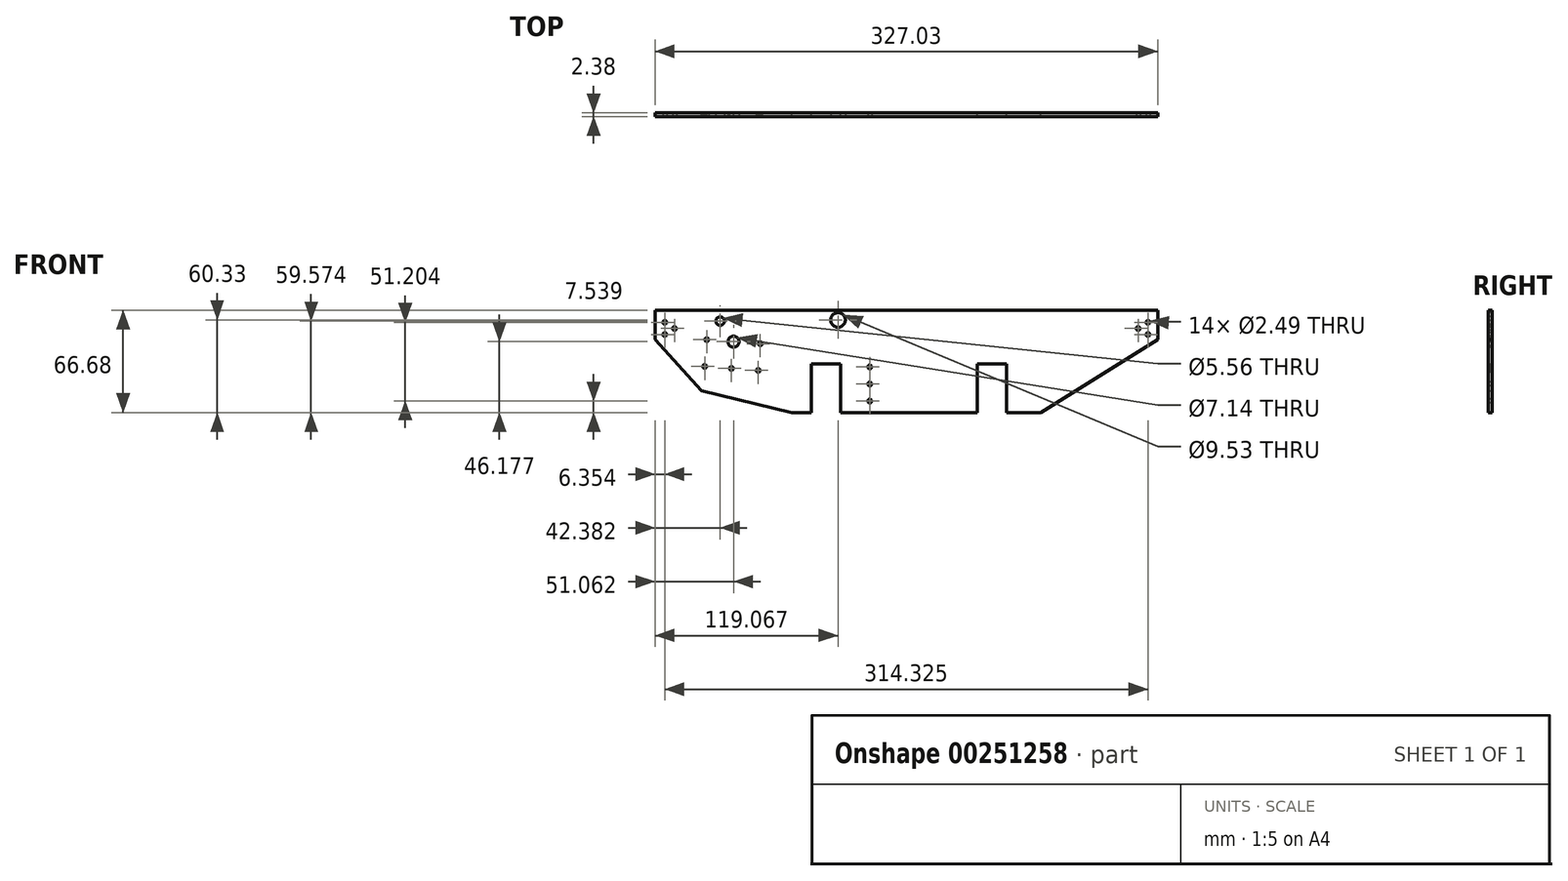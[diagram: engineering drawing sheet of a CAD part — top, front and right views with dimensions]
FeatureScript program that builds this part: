
annotation { "Feature Type Name" : "Feature", "Feature Type Description" : "" }
export const myFeature = defineFeature(function(context is Context, id is Id, definition is map)
    precondition{}
    {
        {
            var Q0;
            Q0=qCreatedBy(makeId("Front.planeOp"),FACE);
            var sketch = newSketch(context, id + "F0", { "sketchPlane" : qUnion([Q0])});
            skLineSegment(sketch, "E0", {"start": v(-44.67, 19.05) * mm, "end": v(282.36, 19.05) * mm});
            skLineSegment(sketch, "E1", {"start": v(282.36, 19.05) * mm, "end": v(282.36, 0) * mm});
            skLineSegment(sketch, "E2", {"start": v(282.36, 0) * mm, "end": v(206.16, -47.63) * mm});
            skLineSegment(sketch, "E3", {"start": v(206.16, -47.63) * mm, "end": v(183.93, -47.63) * mm});
            skLineSegment(sketch, "E4", {"start": v(183.93, -47.63) * mm, "end": v(183.93, -15.88) * mm});
            skLineSegment(sketch, "E5", {"start": v(183.93, -15.88) * mm, "end": v(164.88, -15.88) * mm});
            skLineSegment(sketch, "E6", {"start": v(164.88, -15.88) * mm, "end": v(164.88, -47.63) * mm});
            skLineSegment(sketch, "E7", {"start": v(164.88, -47.63) * mm, "end": v(75.98, -47.63) * mm});
            skLineSegment(sketch, "E8", {"start": v(75.98, -47.63) * mm, "end": v(75.98, -15.88) * mm});
            skLineSegment(sketch, "E9", {"start": v(75.98, -15.88) * mm, "end": v(56.93, -15.88) * mm});
            skLineSegment(sketch, "E10", {"start": v(56.93, -15.88) * mm, "end": v(56.93, -47.63) * mm});
            skLineSegment(sketch, "E11", {"start": v(56.93, -47.63) * mm, "end": v(44.23, -47.63) * mm});
            skLineSegment(sketch, "E12", {"start": v(44.23, -47.63) * mm, "end": v(-14.5, -33.4) * mm});
            skLineSegment(sketch, "E13", {"start": v(-14.5, -33.4) * mm, "end": v(-44.67, 0) * mm});
            skLineSegment(sketch, "E14", {"start": v(-44.67, 0) * mm, "end": v(-44.67, 19.05) * mm});
            skSolve(sketch);
        }
        {
            var Q0;
            Q0 = qSketchRegion(id + "F0", true);
            extrude(context, id + "F1", {"entities" : qUnion([Q0]), "depth" : 2.38 * mm});
        }
        {
            var Q0;
            Q0=makeQuery(id+"F1.opExtrude","CAP_FACE",FACE,{"disambiguationData":[OSD([sQuery(id+"F0.wireOp",EDGE,"E0"),sQuery(id+"F0.wireOp",EDGE,"E1"),sQuery(id+"F0.wireOp",EDGE,"E2"),sQuery(id+"F0.wireOp",EDGE,"E3"),sQuery(id+"F0.wireOp",EDGE,"E4"),sQuery(id+"F0.wireOp",EDGE,"E5"),sQuery(id+"F0.wireOp",EDGE,"E6"),sQuery(id+"F0.wireOp",EDGE,"E7"),sQuery(id+"F0.wireOp",EDGE,"E8"),sQuery(id+"F0.wireOp",EDGE,"E9"),sQuery(id+"F0.wireOp",EDGE,"E10"),sQuery(id+"F0.wireOp",EDGE,"E11"),sQuery(id+"F0.wireOp",EDGE,"E12"),sQuery(id+"F0.wireOp",EDGE,"E13"),sQuery(id+"F0.wireOp",EDGE,"E14")])],"isStart":false});
            var sketch = newSketch(context, id + "F2", { "sketchPlane" : qUnion([Q0])});
            skCircle(sketch, "E15", {"center": v(276, 11.11) * mm, "radius": 1.24 * mm});
            skCircle(sketch, "E16", {"center": v(276, 3.17) * mm, "radius": 1.24 * mm});
            skCircle(sketch, "E17", {"center": v(269.66, 7.14) * mm, "radius": 1.24 * mm});
            skCircle(sketch, "E18", {"center": v(74.4, 12.7) * mm, "radius": 4.76 * mm});
            skCircle(sketch, "E19", {"center": v(95.03, -17.87) * mm, "radius": 1.24 * mm});
            skCircle(sketch, "E20", {"center": v(95.03, -28.98) * mm, "radius": 1.24 * mm});
            skCircle(sketch, "E21", {"center": v(95.03, -40.1) * mm, "radius": 1.24 * mm});
            skCircle(sketch, "E22", {"center": v(-38.32, 11.11) * mm, "radius": 1.24 * mm});
            skCircle(sketch, "E23", {"center": v(-38.32, 3.17) * mm, "radius": 1.24 * mm});
            skCircle(sketch, "E24", {"center": v(-31.97, 7.14) * mm, "radius": 1.24 * mm});
            skPoint(sketch, "E25", {"position": v(174.4, -31.75) * mm});
            skLineSegment(sketch, "E26", {"start": v(174.4, -31.75) * mm, "end": v(-44.67, -15.08) * mm});
            skCircle(sketch, "E27", {"center": v(-12.34, -17.54) * mm, "radius": 1.24 * mm});
            skCircle(sketch, "E28", {"center": v(5.07, -18.87) * mm, "radius": 1.24 * mm});
            skCircle(sketch, "E29", {"center": v(22.48, -20.2) * mm, "radius": 1.24 * mm});
            skCircle(sketch, "E30", {"center": v(-11.02, -0.13) * mm, "radius": 1.24 * mm});
            skCircle(sketch, "E31", {"center": v(23.8, -2.78) * mm, "radius": 1.24 * mm});
            skCircle(sketch, "E32", {"center": v(6.4, -1.45) * mm, "radius": 3.57 * mm});
            skCircle(sketch, "E33", {"center": v(-2.29, 11.94) * mm, "radius": 2.78 * mm});
            skLineSegment(sketch, "E34", {"start": v(-44.67, -15.08) * mm, "end": v(-42.74, 10.26) * mm});
            skLineSegment(sketch, "E35", {"start": v(-12.34, -17.54) * mm, "end": v(-10.66, 4.63) * mm});
            skSolve(sketch);
        }
        {
            var Q0;
            Q0 = qSketchRegion(id + "F2", true);
            extrude(context, id + "F3", {"entities" : qUnion([Q0]), "operationType" : NewBodyOperationType.REMOVE, "oppositeDirection" : true, "depth" : 2.38 * mm});
        }
    });
